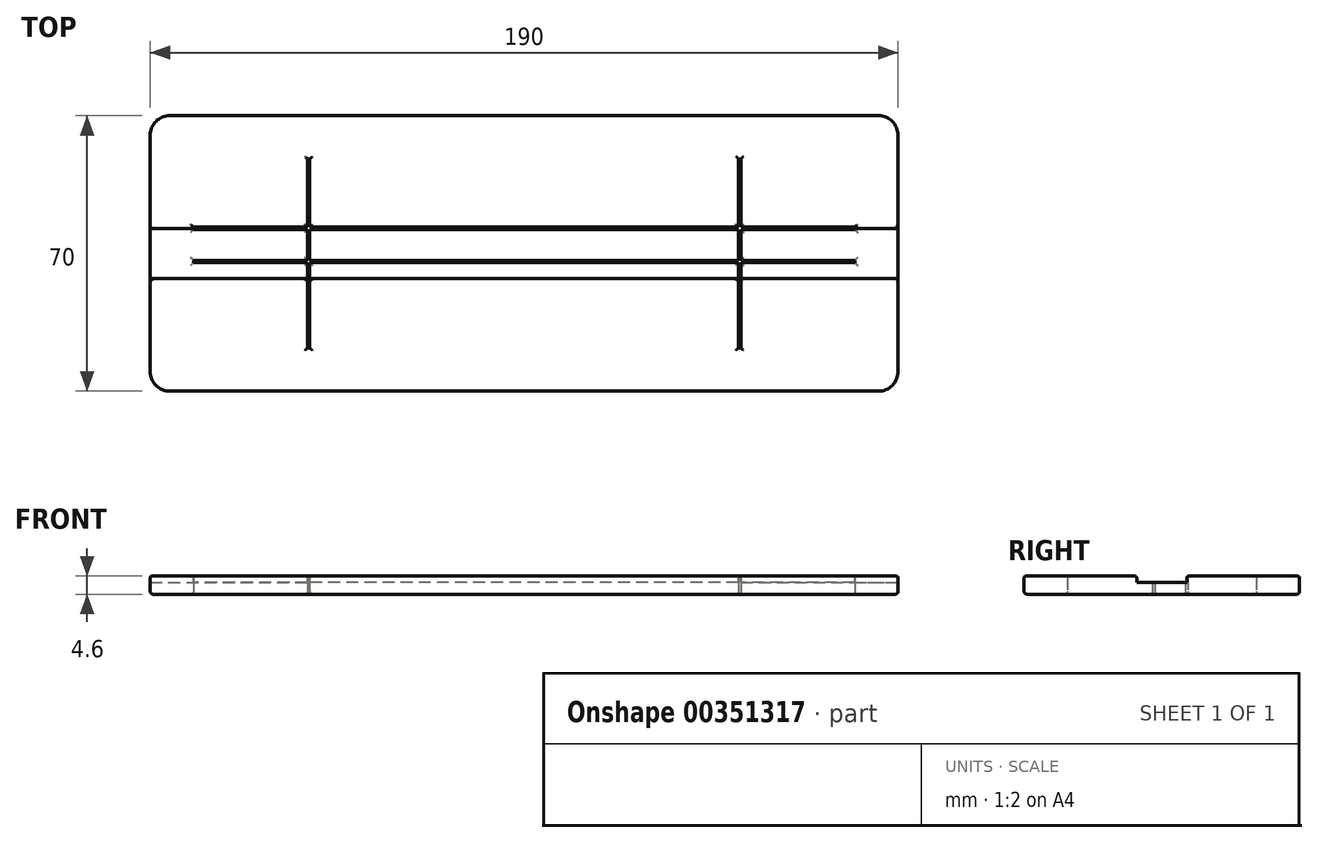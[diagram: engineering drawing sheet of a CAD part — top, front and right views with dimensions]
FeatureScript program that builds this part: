
annotation { "Feature Type Name" : "Feature", "Feature Type Description" : "" }
export const myFeature = defineFeature(function(context is Context, id is Id, definition is map)
    precondition{}
    {
        {
            var Q0;
            Q0=qCreatedBy(makeId("Top.planeOp"),FACE);
            var sketch = newSketch(context, id + "F0", { "sketchPlane" : qUnion([Q0])});
            skLineSegment(sketch, "E0.bottom", {"start": v(-95, 35) * mm, "end": v(95, 35) * mm});
            skLineSegment(sketch, "E0.top", {"start": v(-95, -35) * mm, "end": v(95, -35) * mm});
            skLineSegment(sketch, "E0.left", {"start": v(-95, 35) * mm, "end": v(-95, -35) * mm});
            skLineSegment(sketch, "E0.right", {"start": v(95, 35) * mm, "end": v(95, -35) * mm});
            skSolve(sketch);
        }
        {
            var Q0;
            Q0 = qSketchRegion(id + "F0", true);
            extrude(context, id + "F1", {"entities" : qUnion([Q0]), "depth" : 3 * mm});
        }
        {
            var Q0;
            Q0=makeQuery(id+"F1.opExtrude","CAP_FACE",FACE,{"disambiguationData":[OSD([sQuery(id+"F0.wireOp",EDGE,"E0.bottom"),sQuery(id+"F0.wireOp",EDGE,"E0.top"),sQuery(id+"F0.wireOp",EDGE,"E0.left"),sQuery(id+"F0.wireOp",EDGE,"E0.right")])],"isStart":false});
            var sketch = newSketch(context, id + "F2", { "sketchPlane" : qUnion([Q0])});
            skLineSegment(sketch, "E1.bottom", {"start": v(-95, 35) * mm, "end": v(95, 35) * mm});
            skLineSegment(sketch, "E1.top", {"start": v(-95, 6.35) * mm, "end": v(95, 6.35) * mm});
            skLineSegment(sketch, "E1.left", {"start": v(-95, 35) * mm, "end": v(-95, 6.35) * mm});
            skLineSegment(sketch, "E1.right", {"start": v(95, 35) * mm, "end": v(95, 6.35) * mm});
            skLineSegment(sketch, "E2.bottom", {"start": v(-95, -35) * mm, "end": v(95, -35) * mm});
            skLineSegment(sketch, "E2.top", {"start": v(-95, -6.35) * mm, "end": v(95, -6.35) * mm});
            skLineSegment(sketch, "E2.left", {"start": v(-95, -35) * mm, "end": v(-95, -6.35) * mm});
            skLineSegment(sketch, "E2.right", {"start": v(95, -35) * mm, "end": v(95, -6.35) * mm});
            skSolve(sketch);
        }
        {
            var Q0;
            Q0 = qSketchRegion(id + "F2", true);
            extrude(context, id + "F3", {"entities" : qUnion([Q0]), "operationType" : NewBodyOperationType.ADD, "depth" : 1.6 * mm});
        }
        {
            var Q0;
            Q0=makeQuery(id+"F1.opExtrude","CAP_FACE",FACE,{"disambiguationData":[OSD([sQuery(id+"F0.wireOp",EDGE,"E0.bottom"),sQuery(id+"F0.wireOp",EDGE,"E0.top"),sQuery(id+"F0.wireOp",EDGE,"E0.left"),sQuery(id+"F0.wireOp",EDGE,"E0.right")])],"isStart":true});
            var sketch = newSketch(context, id + "F4", { "sketchPlane" : qUnion([Q0])});
            skLineSegment(sketch, "E3.bottom", {"start": v(-84, 2.35) * mm, "end": v(-55.05, 2.35) * mm});
            skLineSegment(sketch, "E3.top", {"start": v(-84, 1.75) * mm, "end": v(-55.05, 1.75) * mm});
            skLineSegment(sketch, "E3.left", {"start": v(-84, 2.35) * mm, "end": v(-84, 1.75) * mm});
            skLineSegment(sketch, "E3.right", {"start": v(84, 2.35) * mm, "end": v(84, 1.75) * mm});
            skLineSegment(sketch, "E4", {"start": v(-84, 2.05) * mm, "end": v(-69.02, 2.05) * mm, "construction": true});
            skLineSegment(sketch, "E5.bottom", {"start": v(-55.05, 24) * mm, "end": v(-54.45, 24) * mm});
            skLineSegment(sketch, "E5.top", {"start": v(-55.05, -24) * mm, "end": v(-54.45, -24) * mm});
            skLineSegment(sketch, "E5.left", {"start": v(-55.05, 24) * mm, "end": v(-55.05, 2.35) * mm});
            skLineSegment(sketch, "E5.right", {"start": v(-54.45, 24) * mm, "end": v(-54.45, 2.35) * mm});
            skLineSegment(sketch, "E6.bottom", {"start": v(54.45, 24) * mm, "end": v(55.05, 24) * mm});
            skLineSegment(sketch, "E6.top", {"start": v(54.45, -24) * mm, "end": v(55.05, -24) * mm});
            skLineSegment(sketch, "E6.left", {"start": v(54.45, 24) * mm, "end": v(54.45, 2.35) * mm});
            skLineSegment(sketch, "E6.right", {"start": v(55.05, 24) * mm, "end": v(55.05, 2.35) * mm});
            skLineSegment(sketch, "E7", {"start": v(-54.75, 24) * mm, "end": v(-54.75, 15.82) * mm, "construction": true});
            skLineSegment(sketch, "E8", {"start": v(54.75, 24) * mm, "end": v(54.75, 17.5) * mm, "construction": true});
            skLineSegment(sketch, "E9.bottom", {"start": v(-84, -6.05) * mm, "end": v(-55.05, -6.05) * mm});
            skLineSegment(sketch, "E9.top", {"start": v(-84, -6.65) * mm, "end": v(-55.05, -6.65) * mm});
            skLineSegment(sketch, "E9.left", {"start": v(-84, -6.05) * mm, "end": v(-84, -6.65) * mm});
            skLineSegment(sketch, "E9.right", {"start": v(84, -6.05) * mm, "end": v(84, -6.65) * mm});
            skLineSegment(sketch, "E10.trimOffspring", {"start": v(-54.45, 2.35) * mm, "end": v(54.45, 2.35) * mm});
            skLineSegment(sketch, "E11.trimOffspring", {"start": v(-54.45, 1.75) * mm, "end": v(54.45, 1.75) * mm});
            skLineSegment(sketch, "E12.trimOffspring", {"start": v(-54.45, 1.75) * mm, "end": v(-54.45, -6.05) * mm});
            skLineSegment(sketch, "E13.trimOffspring", {"start": v(-55.05, 1.75) * mm, "end": v(-55.05, -6.05) * mm});
            skLineSegment(sketch, "E14.trimOffspring", {"start": v(-54.45, -6.05) * mm, "end": v(54.45, -6.05) * mm});
            skLineSegment(sketch, "E15.trimOffspring", {"start": v(-55.05, -6.65) * mm, "end": v(-55.05, -24) * mm});
            skLineSegment(sketch, "E16.trimOffspring", {"start": v(-54.45, -6.65) * mm, "end": v(54.45, -6.65) * mm});
            skLineSegment(sketch, "E17.trimOffspring", {"start": v(-54.45, -6.65) * mm, "end": v(-54.45, -24) * mm});
            skLineSegment(sketch, "E18.trimOffspring", {"start": v(55.05, 2.35) * mm, "end": v(84, 2.35) * mm});
            skLineSegment(sketch, "E19.trimOffspring", {"start": v(55.05, 1.75) * mm, "end": v(84, 1.75) * mm});
            skLineSegment(sketch, "E20.trimOffspring", {"start": v(55.05, 1.75) * mm, "end": v(55.05, -6.05) * mm});
            skLineSegment(sketch, "E21.trimOffspring", {"start": v(54.45, 1.75) * mm, "end": v(54.45, -6.05) * mm});
            skLineSegment(sketch, "E22.trimOffspring", {"start": v(55.05, -6.05) * mm, "end": v(84, -6.05) * mm});
            skLineSegment(sketch, "E23.trimOffspring", {"start": v(54.45, -6.65) * mm, "end": v(54.45, -24) * mm});
            skLineSegment(sketch, "E24.trimOffspring", {"start": v(55.05, -6.65) * mm, "end": v(84, -6.65) * mm});
            skLineSegment(sketch, "E25.trimOffspring", {"start": v(55.05, -6.65) * mm, "end": v(55.05, -24) * mm});
            skSolve(sketch);
        }
        {
            var Q0;
            Q0 = qSketchRegion(id + "F4", true);
            extrude(context, id + "F5", {"entities" : qUnion([Q0]), "operationType" : NewBodyOperationType.REMOVE, "oppositeDirection" : true, "depth" : 25 * mm});
        }
        {
            var Q0;
            Q0=makeQuery(id+"F3.boolean.opBoolean","MERGE",EDGE,{"derivedFrom":[makeQuery(id+"F1.opExtrude","SWEPT_EDGE",EDGE,{"disambiguationData":[OSD([sQuery(id+"F0.wireOp",EDGE,"E0.bottom"),sQuery(id+"F0.wireOp",EDGE,"E0.right")])]}),makeQuery(id+"F3.opExtrude","SWEPT_EDGE",EDGE,{"disambiguationData":[OSD([sQuery(id+"F2.wireOp",EDGE,"E1.bottom"),sQuery(id+"F2.wireOp",EDGE,"E1.right")])]})]});
            var Q1;
            Q1=makeQuery(id+"F3.boolean.opBoolean","MERGE",EDGE,{"derivedFrom":[makeQuery(id+"F1.opExtrude","SWEPT_EDGE",EDGE,{"disambiguationData":[OSD([sQuery(id+"F0.wireOp",EDGE,"E0.top"),sQuery(id+"F0.wireOp",EDGE,"E0.right")])]}),makeQuery(id+"F3.opExtrude","SWEPT_EDGE",EDGE,{"disambiguationData":[OSD([sQuery(id+"F2.wireOp",EDGE,"E2.bottom"),sQuery(id+"F2.wireOp",EDGE,"E2.right")])]})]});
            var Q2;
            Q2=makeQuery(id+"F3.boolean.opBoolean","MERGE",EDGE,{"derivedFrom":[makeQuery(id+"F1.opExtrude","SWEPT_EDGE",EDGE,{"disambiguationData":[OSD([sQuery(id+"F0.wireOp",EDGE,"E0.top"),sQuery(id+"F0.wireOp",EDGE,"E0.left")])]}),makeQuery(id+"F3.opExtrude","SWEPT_EDGE",EDGE,{"disambiguationData":[OSD([sQuery(id+"F2.wireOp",EDGE,"E2.bottom"),sQuery(id+"F2.wireOp",EDGE,"E2.left")])]})]});
            var Q3;
            Q3=makeQuery(id+"F3.boolean.opBoolean","MERGE",EDGE,{"derivedFrom":[makeQuery(id+"F1.opExtrude","SWEPT_EDGE",EDGE,{"disambiguationData":[OSD([sQuery(id+"F0.wireOp",EDGE,"E0.bottom"),sQuery(id+"F0.wireOp",EDGE,"E0.left")])]}),makeQuery(id+"F3.opExtrude","SWEPT_EDGE",EDGE,{"disambiguationData":[OSD([sQuery(id+"F2.wireOp",EDGE,"E1.bottom"),sQuery(id+"F2.wireOp",EDGE,"E1.left")])]})]});
            fillet(context, id + "F6", {"entities" : qUnion([Q0, Q1, Q2, Q3]), "radius" : 5 * mm, "tangentPropagation" : true, "allowEdgeOverflow" : false});
        }
        {
            var Q0;
            {var subQ0=sQuery(id+"F0.wireOp",EDGE,"E0.bottom");var subQ1=sQuery(id+"F0.wireOp",EDGE,"E0.top");var subQ2=sQuery(id+"F0.wireOp",EDGE,"E0.right");var subQ3=sQuery(id+"F0.wireOp",EDGE,"E0.left");Q0=makeQuery(id+"F5.boolean.opBoolean","SPLIT",FACE,{"disambiguationData":[TD([makeQuery(id+"F1.opExtrude","SWEPT_FACE",FACE,{"disambiguationData":[OSD([subQ0])]})])],"derivedFrom":makeQuery(id+"F1.opExtrude","CAP_FACE",FACE,{"disambiguationData":[OSD([subQ0,subQ1,subQ3,subQ2])],"isStart":true})});}
            fillet(context, id + "F7", {"entities" : qUnion([Q0]), "radius" : .75 * mm, "tangentPropagation" : true, "allowEdgeOverflow" : false});
        }
        {
            var Q0;
            Q0=makeQuery(id+"F3.opExtrude","CAP_FACE",FACE,{"disambiguationData":[OSD([sQuery(id+"F2.wireOp",EDGE,"E2.bottom"),sQuery(id+"F2.wireOp",EDGE,"E2.top"),sQuery(id+"F2.wireOp",EDGE,"E2.left"),sQuery(id+"F2.wireOp",EDGE,"E2.right")])],"isStart":false});
            var Q1;
            Q1=makeQuery(id+"F3.opExtrude","CAP_FACE",FACE,{"disambiguationData":[OSD([sQuery(id+"F2.wireOp",EDGE,"E1.bottom"),sQuery(id+"F2.wireOp",EDGE,"E1.top"),sQuery(id+"F2.wireOp",EDGE,"E1.left"),sQuery(id+"F2.wireOp",EDGE,"E1.right")])],"isStart":false});
            fillet(context, id + "F8", {"entities" : qUnion([Q0, Q1]), "radius" : .5 * mm, "tangentPropagation" : true, "allowEdgeOverflow" : false});
        }
    });
